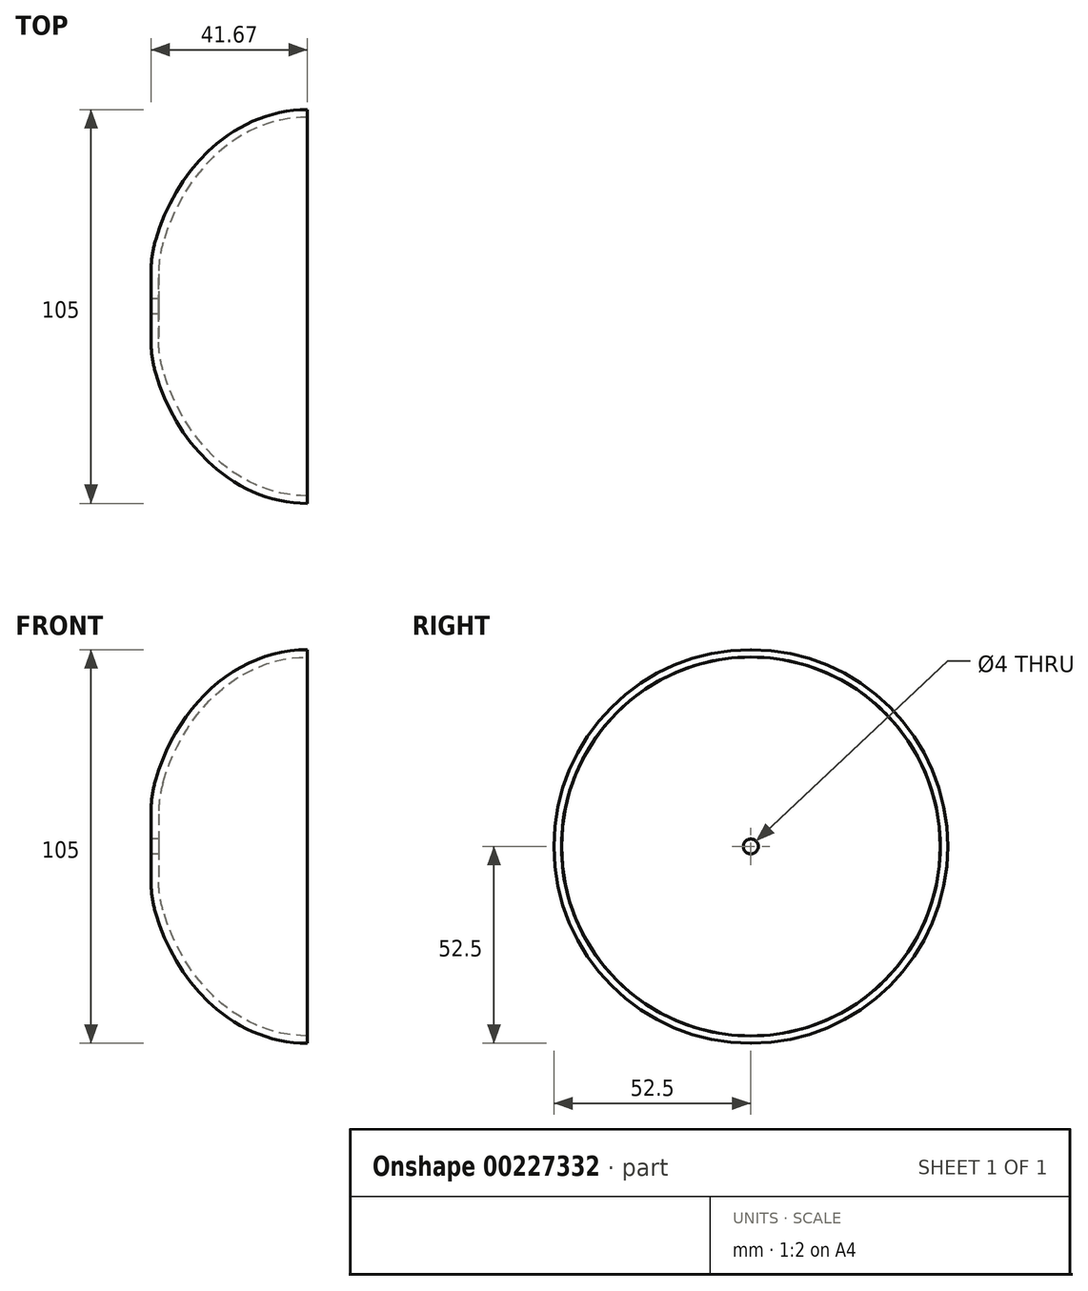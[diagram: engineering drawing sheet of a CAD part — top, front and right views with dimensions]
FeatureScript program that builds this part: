
annotation { "Feature Type Name" : "Feature", "Feature Type Description" : "" }
export const myFeature = defineFeature(function(context is Context, id is Id, definition is map)
    precondition{}
    {
        {
            var Q0;
            Q0=qCreatedBy(makeId("Top.planeOp"),FACE);
            var sketch = newSketch(context, id + "F0", { "sketchPlane" : qUnion([Q0])});
            skEllipticalArc(sketch, "E0", {});
            skLineSegment(sketch, "E1", {"start": v(0, -52.5) * mm, "end": v(0, -50.5) * mm});
            skEllipticalArc(sketch, "E2", {});
            skLineSegment(sketch, "E3", {"start": v(-41.67, 0) * mm, "end": v(-40.88, 0) * mm});
            skLineSegment(sketch, "E4", {"start": v(-41.67, -9.33) * mm, "end": v(-41.67, 0) * mm});
            skLineSegment(sketch, "E5", {"start": v(-40.88, 0) * mm, "end": v(-39.67, 0) * mm});
            skLineSegment(sketch, "E6", {"start": v(-39.67, 0) * mm, "end": v(-39.67, -8.67) * mm});
            skPoint(sketch, "E7.visualSharp", {"position": v(-41.67, -12.95) * mm});
            skArc(sketch, "E7.filletArc", {"start": v(-41.67, -9.33) * mm, "mid": v(-41.36, -13.64) * mm, "end": v(-40.44, -17.86) * mm});
            skPoint(sketch, "E8.visualSharp", {"position": v(-39.67, -12.18) * mm});
            skArc(sketch, "E8.filletArc", {"start": v(-39.67, -8.67) * mm, "mid": v(-39.37, -12.89) * mm, "end": v(-38.49, -17.02) * mm});
            skLineSegment(sketch, "E9", {"start": v(-39.67, 0) * mm, "end": v(-23.97, 0) * mm});
            const initialGuessF0  = {"E0": [0, 0, 0, 1, 0.0525, 0.043, 1.91782595262061, 3.141592653589793], "E2": [0, 0, 0, -1, 0.0505, 0.04087881200984811, 5.056210640097931, 0]};
            skSetInitialGuess(sketch, initialGuessF0);
            skSolve(sketch);
        }
        {
            var Q0;
            Q0=makeQuery(id+"F0.imprint","IMPRINT",FACE,{"disambiguationData":[TD([[makeQuery(id+"F0.imprint","IMPRINT",EDGE,{"derivedFrom":sQuery(id+"F0.wireOp",EDGE,"E0")}),1.0]])]});
            var Q1;
            Q1=sQuery(id+"F0.wireOp",EDGE,"E9");
            revolve(context, id + "F1", {"entities" : qUnion([Q0]), "axis" : qUnion([Q1]), "revolveType" : RevolveType.FULL});
        }
        {
            var Q0;
            Q0=makeQuery(id+"F1.opRevolve","SWEPT_FACE",FACE,{"disambiguationData":[OSD([sQuery(id+"F0.wireOp",EDGE,"E4")])]});
            var sketch = newSketch(context, id + "F2", { "sketchPlane" : qUnion([Q0])});
            skCircle(sketch, "E10", {"center": v(0, 0) * mm, "radius": 2 * mm});
            skSolve(sketch);
        }
        {
            var Q0;
            Q0=makeQuery(id+"F2.imprint","IMPRINT",FACE,{"disambiguationData":[TD([[makeQuery(id+"F2.imprint","IMPRINT",EDGE,{"derivedFrom":sQuery(id+"F2.wireOp",EDGE,"E10")}),1.0]])]});
            extrude(context, id + "F3", {"entities" : qUnion([Q0]), "operationType" : NewBodyOperationType.REMOVE, "oppositeDirection" : true, "depth" : 25 * mm});
        }
    });
